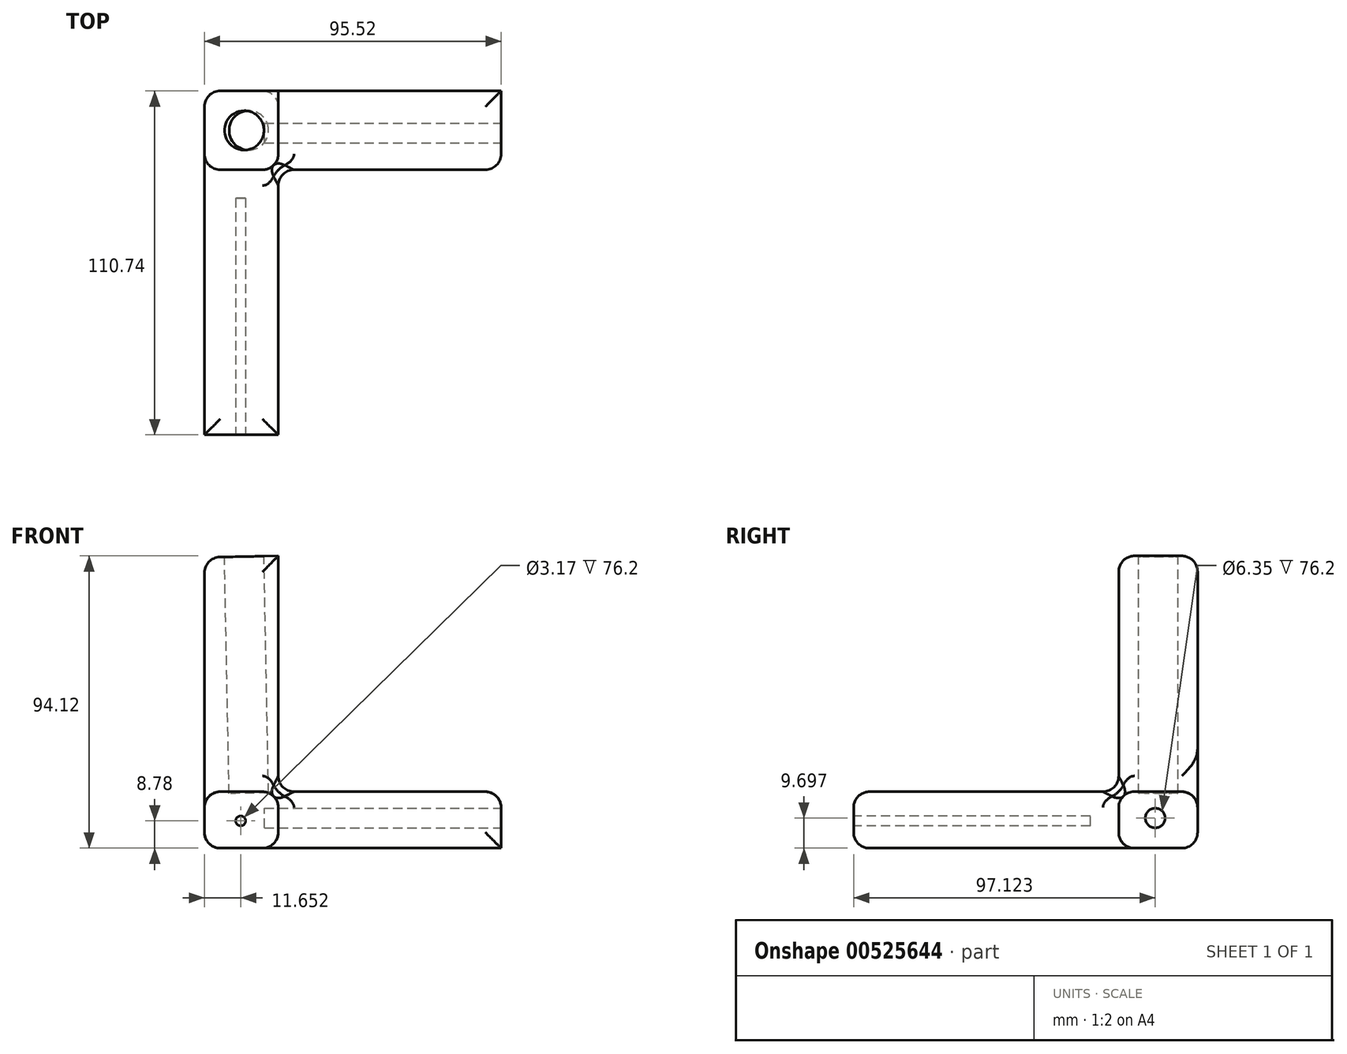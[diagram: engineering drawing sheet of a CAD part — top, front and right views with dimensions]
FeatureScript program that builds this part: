
annotation { "Feature Type Name" : "Feature", "Feature Type Description" : "" }
export const myFeature = defineFeature(function(context is Context, id is Id, definition is map)
    precondition{}
    {
        {
            var Q0;
            Q0=qCreatedBy(makeId("Front.planeOp"),FACE);
            var sketch = newSketch(context, id + "F0", { "sketchPlane" : qUnion([Q0])});
            skLineSegment(sketch, "E0", {"start": v(0, 93.65) * mm, "end": v(0, 0) * mm});
            skLineSegment(sketch, "E1", {"start": v(0, 0) * mm, "end": v(95.52, 0) * mm});
            skLineSegment(sketch, "E2", {"start": v(23.76, 94.12) * mm, "end": v(23.76, 18.17) * mm});
            skLineSegment(sketch, "E3", {"start": v(23.76, 18.17) * mm, "end": v(95.52, 18.17) * mm});
            skLineSegment(sketch, "E4", {"start": v(95.52, 18.17) * mm, "end": v(95.52, 0) * mm});
            skLineSegment(sketch, "E5", {"start": v(23.76, 94.12) * mm, "end": v(0, 93.65) * mm});
            skSolve(sketch);
        }
        {
            var Q0;
            Q0 = qSketchRegion(id + "F0", true);
            extrude(context, id + "F1", {"entities" : qUnion([Q0]), "oppositeDirection" : true, "depth" : 25.4 * mm, "offsetDistance" : 25.4 * mm});
        }
        {
            var Q0;
            Q0=makeQuery(id+"F1.opExtrude","CAP_FACE",FACE,{"disambiguationData":[OSD([sQuery(id+"F0.wireOp",EDGE,"E0"),sQuery(id+"F0.wireOp",EDGE,"E1"),sQuery(id+"F0.wireOp",EDGE,"E2"),sQuery(id+"F0.wireOp",EDGE,"E3"),sQuery(id+"F0.wireOp",EDGE,"E4"),sQuery(id+"F0.wireOp",EDGE,"E5")])],"isStart":true});
            var sketch = newSketch(context, id + "F2", { "sketchPlane" : qUnion([Q0])});
            skLineSegment(sketch, "E6", {"start": v(23.76, 18.17) * mm, "end": v(0, 18.17) * mm});
            skLineSegment(sketch, "E7", {"start": v(0, 0) * mm, "end": v(23.76, 0) * mm});
            skLineSegment(sketch, "E8", {"start": v(23.76, 0) * mm, "end": v(23.76, 18.17) * mm});
            skLineSegment(sketch, "E9", {"start": v(0, 18.17) * mm, "end": v(0, 0) * mm});
            skSolve(sketch);
        }
        {
            var Q0;
            Q0 = qSketchRegion(id + "F2", true);
            extrude(context, id + "F3", {"entities" : qUnion([Q0]), "operationType" : NewBodyOperationType.ADD, "depth" : 85.34 * mm, "offsetDistance" : 25.4 * mm});
        }
        {
            var Q0;
            Q0=makeQuery(id+"F1.opExtrude","SWEPT_FACE",FACE,{"disambiguationData":[OSD([sQuery(id+"F0.wireOp",EDGE,"E5")])]});
            var sketch = newSketch(context, id + "F4", { "sketchPlane" : qUnion([Q0])});
            skCircle(sketch, "E10", {"center": v(14.64, 12.7) * mm, "radius": 6.35 * mm});
            skPoint(sketch, "E10.centerSnap0", {"position": v(1.84, 12.7) * mm});
            skSolve(sketch);
        }
        {
            var Q0;
            Q0=makeQuery(id+"F4.imprint","IMPRINT",FACE,{"disambiguationData":[TD([[makeQuery(id+"F4.imprint","IMPRINT",EDGE,{"derivedFrom":sQuery(id+"F4.wireOp",EDGE,"E10")}),1.0]])]});
            var Q1;
            Q1=sQuery(id+"F4.wireOp",EDGE,"E10");
            extrude(context, id + "F5", {"entities" : qUnion([Q0]), "operationType" : NewBodyOperationType.REMOVE, "surfaceEntities" : qUnion([Q1]), "endBound" : BoundingType.SYMMETRIC, "oppositeDirection" : true, "depth" : 152.4 * mm, "offsetDistance" : 25.4 * mm});
        }
        {
            var Q0;
            Q0=makeQuery(id+"F1.opExtrude","SWEPT_FACE",FACE,{"disambiguationData":[OSD([sQuery(id+"F0.wireOp",EDGE,"E4")])]});
            var sketch = newSketch(context, id + "F6", { "sketchPlane" : qUnion([Q0])});
            skCircle(sketch, "E11", {"center": v(11.78, 9.7) * mm, "radius": 3.17 * mm});
            skSolve(sketch);
        }
        {
            var Q0;
            Q0 = qSketchRegion(id + "F6", true);
            extrude(context, id + "F7", {"entities" : qUnion([Q0]), "operationType" : NewBodyOperationType.REMOVE, "oppositeDirection" : true, "depth" : 76.2 * mm, "offsetDistance" : 25.4 * mm});
        }
        {
            var Q0;
            Q0=makeQuery(id+"F3.opExtrude","CAP_FACE",FACE,{"disambiguationData":[OSD([sQuery(id+"F2.wireOp",EDGE,"E6"),sQuery(id+"F2.wireOp",EDGE,"E7"),sQuery(id+"F2.wireOp",EDGE,"E8"),sQuery(id+"F2.wireOp",EDGE,"E9")])],"isStart":false});
            var sketch = newSketch(context, id + "F8", { "sketchPlane" : qUnion([Q0])});
            skCircle(sketch, "E12", {"center": v(11.65, 8.78) * mm, "radius": 1.59 * mm});
            skSolve(sketch);
        }
        {
            var Q0;
            Q0 = qSketchRegion(id + "F8", true);
            extrude(context, id + "F9", {"entities" : qUnion([Q0]), "operationType" : NewBodyOperationType.REMOVE, "oppositeDirection" : true, "depth" : 76.2 * mm, "offsetDistance" : 25.4 * mm});
        }
        {
            var Q0;
            {var subQ0=sQuery(id+"F0.wireOp",EDGE,"E2");var subQ1=sQuery(id+"F0.wireOp",EDGE,"E5");var subQ2=sQuery(id+"F0.wireOp",EDGE,"E3");var subQ3=sQuery(id+"F0.wireOp",EDGE,"E0");var subQ4=makeQuery(id+"F1.opExtrude","CAP_FACE",FACE,{"disambiguationData":[OSD([subQ3,sQuery(id+"F0.wireOp",EDGE,"E1"),subQ0,subQ2,sQuery(id+"F0.wireOp",EDGE,"E4"),subQ1])],"isStart":true});Q0=makeQuery(id+"F3.boolean.opBoolean","SPLIT",FACE,{"disambiguationData":[TD([makeQuery(id+"F1.opExtrude","SWEPT_FACE",FACE,{"disambiguationData":[OSD([subQ3])]})])],"derivedFrom":subQ4});}
            var Q1;
            Q1=makeQuery(id+"F3.opExtrude","SWEPT_FACE",FACE,{"disambiguationData":[OSD([sQuery(id+"F2.wireOp",EDGE,"E6")])]});
            var Q2;
            Q2=makeQuery(id+"F1.opExtrude","SWEPT_FACE",FACE,{"disambiguationData":[OSD([sQuery(id+"F0.wireOp",EDGE,"E3")])]});
            var Q3;
            Q3=makeQuery(id+"F3.opExtrude","SWEPT_EDGE",EDGE,{"disambiguationData":[OSD([sQuery(id+"F0.wireOp",EDGE,"E1"),sQuery(id+"F2.wireOp",EDGE,"E7"),sQuery(id+"F2.wireOp",EDGE,"E8")])]});
            var Q4;
            {var subQ0=sQuery(id+"F0.wireOp",EDGE,"E3");var subQ1=sQuery(id+"F0.wireOp",EDGE,"E2");var subQ2=sQuery(id+"F0.wireOp",EDGE,"E1");var subQ3=sQuery(id+"F0.wireOp",EDGE,"E4");var subQ4=makeQuery(id+"F1.opExtrude","CAP_FACE",FACE,{"disambiguationData":[OSD([sQuery(id+"F0.wireOp",EDGE,"E0"),subQ2,subQ1,subQ0,subQ3,sQuery(id+"F0.wireOp",EDGE,"E5")])],"isStart":true});Q4=makeQuery(id+"F3.boolean.opBoolean","SPLIT",FACE,{"disambiguationData":[TD([makeQuery(id+"F1.opExtrude","SWEPT_FACE",FACE,{"disambiguationData":[OSD([subQ2])]})])],"derivedFrom":subQ4});}
            var Q5;
            Q5=makeQuery(id+"F1.opExtrude","CAP_EDGE",EDGE,{"disambiguationData":[OSD([sQuery(id+"F0.wireOp",EDGE,"E0")])],"isStart":false});
            var Q6;
            Q6=makeQuery(id+"F1.opExtrude","CAP_EDGE",EDGE,{"disambiguationData":[OSD([sQuery(id+"F0.wireOp",EDGE,"E1")])],"isStart":false});
            var Q7;
            Q7=makeQuery(id+"F3.boolean.opBoolean","MERGE",EDGE,{"derivedFrom":[makeQuery(id+"F1.opExtrude","SWEPT_EDGE",EDGE,{"disambiguationData":[OSD([sQuery(id+"F0.wireOp",EDGE,"E0"),sQuery(id+"F0.wireOp",EDGE,"E1")])]}),makeQuery(id+"F3.opExtrude","SWEPT_EDGE",EDGE,{"disambiguationData":[OSD([sQuery(id+"F2.wireOp",EDGE,"E7"),sQuery(id+"F2.wireOp",EDGE,"E9")])]})]});
            var Q8;
            Q8=makeQuery(id+"F3.opExtrude","CAP_EDGE",EDGE,{"disambiguationData":[OSD([sQuery(id+"F2.wireOp",EDGE,"E7")])],"isStart":false});
            var Q9;
            Q9=makeQuery(id+"F1.opExtrude","CAP_EDGE",EDGE,{"disambiguationData":[OSD([sQuery(id+"F0.wireOp",EDGE,"E5")])],"isStart":false});
            var Q10;
            Q10=makeQuery(id+"F1.opExtrude","SWEPT_EDGE",EDGE,{"disambiguationData":[OSD([sQuery(id+"F0.wireOp",EDGE,"E0"),sQuery(id+"F0.wireOp",EDGE,"E5")])]});
            fillet(context, id + "F10", {"entities" : qUnion([Q0, Q1, Q2, Q3, Q4, Q5, Q6, Q7, Q8, Q9, Q10]), "radius" : 5.08 * mm, "tangentPropagation" : true, "allowEdgeOverflow" : false});
        }
    });
